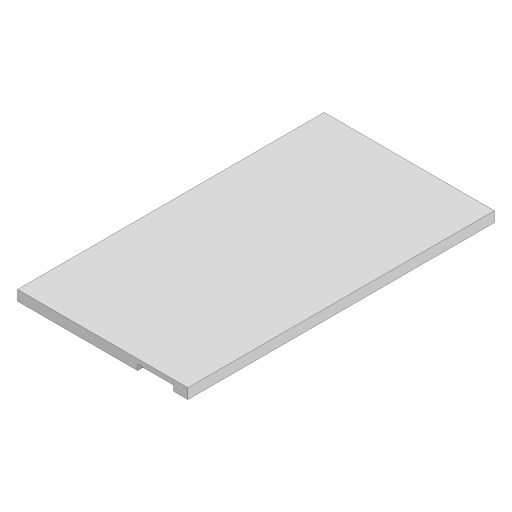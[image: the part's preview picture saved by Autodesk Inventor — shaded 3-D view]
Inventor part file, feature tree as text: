
AUTODESK INVENTOR PART (.ipt)
format: ipt  version: 2024 (Build 280153000, 153)  size: 239,104 bytes
history: native  units: mm
features: extrude x7, sketch x7, projected_geometry x7
ambient origin geometry x8: Origin, YZ Plane, XZ Plane, XY Plane, X Axis, Y Axis, Z Axis, Center Point
bodies: Solid1 (feature_tree)
feature tree (21):
  extrude  "Extrusion1"  Depth=180.0mm
  extrude  "Extrusion2"  Depth=4.0mm
  extrude  "Extrusion3"  Depth=4.0mm TaperAngle=0.0deg
  extrude  "Extrusion4"  Depth=4.0mm
  extrude  "Extrusion5"  Depth=4.0mm
  extrude  "Extrusion6"  Depth=55.0mm
  extrude  "Extrusion7"  Depth=3.2mm
  sketch  "Sketch1"  dims[d0=100.0mm d1=180.0mm]
  sketch  "Sketch2"  dims[d2=4.0mm d3=0.0mm d4=4.0mm]
  sketch  "Sketch3"  dims[d5=4.0mm d6=5.0mm d7=0.0mm]
  sketch  "Sketch4"  dims[d8=30.0mm d9=4.0mm]
  projected_geometry  "Projected Loop1"
  projected_geometry  "Projected Loop2"
  projected_geometry  "Projected Loop3"
  sketch  "Sketch5"  dims[d10=4.0mm d11=4.0mm]
  projected_geometry  "Projected Loop4"
  projected_geometry  "Projected Loop5"
  projected_geometry  "Projected Loop6"
  sketch  "Sketch6"  dims[d12=25.0mm d13=0.0mm d14=55.0mm]
  sketch  "Sketch7"  dims[d15=110.0mm d16=10.0mm d17=20.0mm d18=3.0mm d19=0.0mm d20=3.2mm d21=0.0mm d22=0.5mm d23=0.5mm d24=0.5mm d25=0.5mm d26=0.5mm d27=0.5mm d28=10.0mm d29=0.0mm d30=2.0mm d31=0.0mm]
  projected_geometry  "Projected Loop7"
